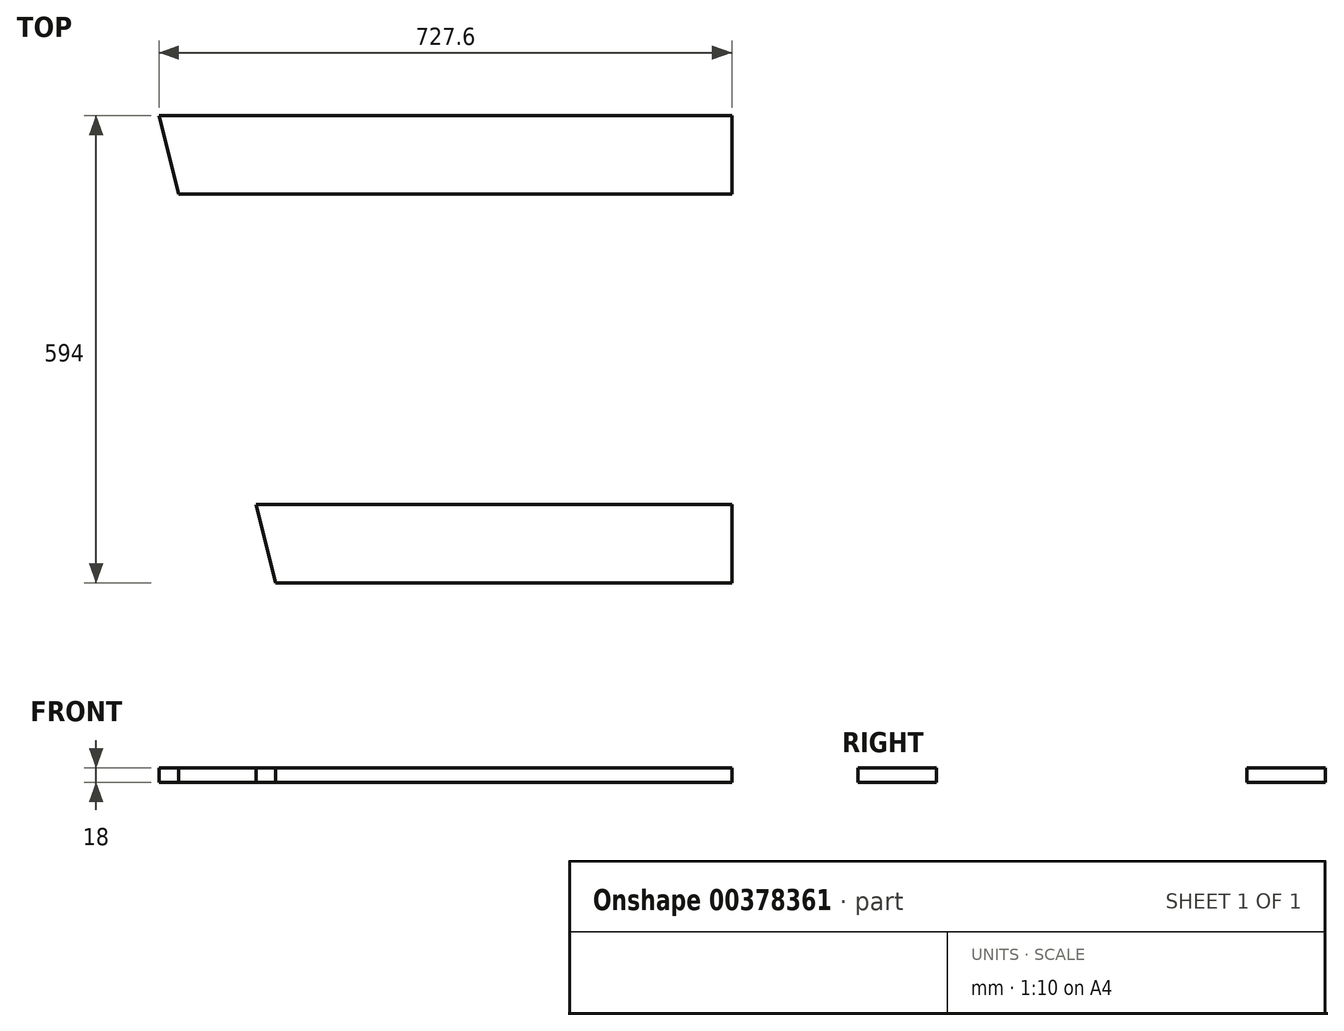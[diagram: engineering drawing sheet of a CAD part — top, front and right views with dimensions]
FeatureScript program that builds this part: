
annotation { "Feature Type Name" : "Feature", "Feature Type Description" : "" }
export const myFeature = defineFeature(function(context is Context, id is Id, definition is map)
    precondition{}
    {
        {
            var Q0;
            Q0=qCreatedBy(makeId("Top.planeOp"),FACE);
            var sketch = newSketch(context, id + "F0", { "sketchPlane" : qUnion([Q0])});
            skLineSegment(sketch, "E0.bottom", {"start": v(289.75, 297) * mm, "end": v(-437.85, 297) * mm});
            skLineSegment(sketch, "E0.top", {"start": v(289.75, -297) * mm, "end": v(-289.75, -297) * mm});
            skLineSegment(sketch, "E0.left", {"start": v(289.75, 297) * mm, "end": v(289.75, 197) * mm});
            skPoint(sketch, "E0.middle", {"position": v(0, 0) * mm});
            skLineSegment(sketch, "E1", {"start": v(-289.75, -297) * mm, "end": v(-314.68, -197) * mm});
            skPoint(sketch, "E0.right.start.orphan", {"position": v(-289.75, 297) * mm});
            skLineSegment(sketch, "E2.0", {"start": v(289.75, 197) * mm, "end": v(-412.92, 197) * mm});
            skLineSegment(sketch, "E3.0", {"start": v(289.75, -197) * mm, "end": v(-314.68, -197) * mm});
            skLineSegment(sketch, "E4.trimOffspring", {"start": v(-412.92, 197) * mm, "end": v(-437.85, 297) * mm});
            skLineSegment(sketch, "E5.trimOffspring", {"start": v(289.75, -197) * mm, "end": v(289.75, -297) * mm});
            skSolve(sketch);
        }
        {
            var Q0;
            Q0 = qSketchRegion(id + "F0", true);
            extrude(context, id + "F1", {"entities" : qUnion([Q0]), "depth" : 18 * mm});
        }
    });
